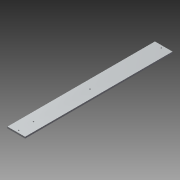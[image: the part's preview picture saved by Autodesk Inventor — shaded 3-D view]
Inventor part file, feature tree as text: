
AUTODESK INVENTOR PART (.ipt)
format: ipt  version: 2015 (Build 190159000, 159)  size: 94,720 bytes
history: native  units: mm
features: reference x4, sketch x2, extrude x1, hole x1
ambient origin geometry x8: Origin, YZ Plane, XZ Plane, XY Plane, X Axis, Y Axis, Z Axis, Center Point
bodies: Solid1 (feature_tree)
feature tree (8):
  extrude  "Extrusion1"  Depth=6.35mm
  hole  "Hole1"  [1 undecoded]
  sketch  "Sketch1"  dims[d0=6.35mm d1=0.0mm d2=20.0mm]
  reference  "Reference1"
  reference  "Reference2"
  reference  "Reference3"
  reference  "Reference4"
  sketch  "Sketch2"  dims[d3=140.0mm d4=20.0mm d5=4.5mm d6=6.0mm d7=8.0mm d8=4.0mm d9=90.0deg d10=8.0mm d11=20.594885mm]
note: 1 required parameter value undecoded (feature->parameter linkage not recoverable at this tier; creation-order binding heuristic only, values carry confidence <= 0.55)
